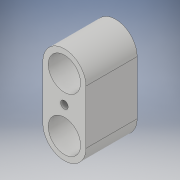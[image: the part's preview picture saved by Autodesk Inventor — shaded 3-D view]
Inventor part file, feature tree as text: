
AUTODESK INVENTOR PART (.ipt)
format: ipt  version: 2019 (Build 230136000, 136)  size: 111,616 bytes
history: native  units: mm
features: other x1, extrude x1, sketch x1
ambient origin geometry x8: Origin, YZ Plane, XZ Plane, XY Plane, X Axis, Y Axis, Z Axis, Center Point
bodies: Body1 (feature_tree)
feature tree (3):
  other  "Твердое тело1"
  extrude  "Выдавливание1"  Depth=12.0mm
  sketch  "Эскиз1"
